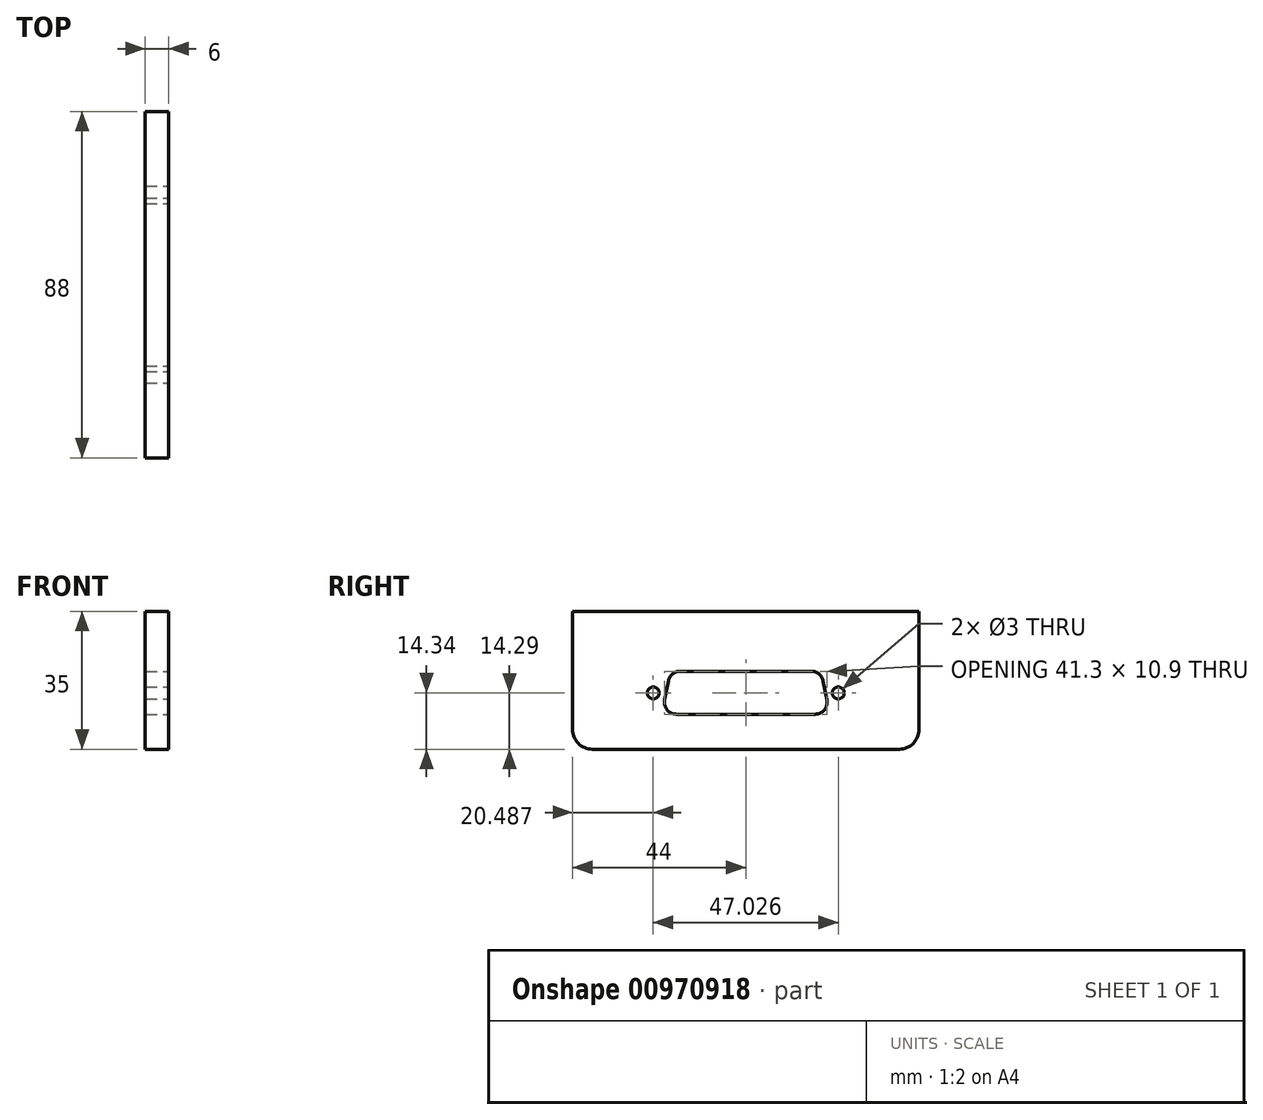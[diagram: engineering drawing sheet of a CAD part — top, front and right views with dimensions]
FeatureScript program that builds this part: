
annotation { "Feature Type Name" : "Feature", "Feature Type Description" : "" }
export const myFeature = defineFeature(function(context is Context, id is Id, definition is map)
    precondition{}
    {
        {
            var Q0;
            Q0=qCreatedBy(makeId("Right.planeOp"),FACE);
            var sketch = newSketch(context, id + "F0", { "sketchPlane" : qUnion([Q0])});
            skLineSegment(sketch, "E0", {"start": v(-81, 2.43) * mm, "end": v(-84.5, 2.43) * mm});
            skLineSegment(sketch, "E1", {"start": v(-84.5, 2.43) * mm, "end": v(-84.5, -12.07) * mm});
            skLineSegment(sketch, "E2", {"start": v(-84.5, -19.57) * mm, "end": v(-84.5, -27.57) * mm});
            skLineSegment(sketch, "E3", {"start": v(-79.5, -32.57) * mm, "end": v(-1.5, -32.57) * mm});
            skLineSegment(sketch, "E4", {"start": v(-81, -29.07) * mm, "end": v(0, -29.07) * mm, "construction": true});
            skLineSegment(sketch, "E5", {"start": v(3.5, 2.43) * mm, "end": v(0, 2.43) * mm});
            skPoint(sketch, "E6.visualSharp", {"position": v(-84.5, -32.57) * mm});
            skArc(sketch, "E6.filletArc", {"start": v(-84.5, -27.57) * mm, "mid": v(-83.04, -31.1) * mm, "end": v(-79.5, -32.57) * mm});
            skLineSegment(sketch, "E7", {"start": v(3.5, 2.43) * mm, "end": v(3.5, -10.57) * mm});
            skLineSegment(sketch, "E8", {"start": v(3.5, -27.57) * mm, "end": v(3.5, -19.57) * mm});
            skLineSegment(sketch, "E9", {"start": v(0, 2.43) * mm, "end": v(0, -29.07) * mm, "construction": true});
            skLineSegment(sketch, "E10", {"start": v(-81, 2.43) * mm, "end": v(0, 2.43) * mm});
            skLineSegment(sketch, "E11", {"start": v(-84.5, -12.07) * mm, "end": v(-84.5, -19.57) * mm});
            skLineSegment(sketch, "E12", {"start": v(3.5, -10.57) * mm, "end": v(3.5, -19.57) * mm});
            skPoint(sketch, "E13.visualSharp", {"position": v(3.5, -32.57) * mm});
            skArc(sketch, "E13.filletArc", {"start": v(-1.5, -32.57) * mm, "mid": v(2.04, -31.1) * mm, "end": v(3.5, -27.57) * mm});
            skLineSegment(sketch, "E14", {"start": v(-81, -29.07) * mm, "end": v(-81, 2.43) * mm, "construction": true});
            skLineSegment(sketch, "E15", {"start": v(-67.01, -12.08) * mm, "end": v(-67.01, -24.48) * mm});
            skLineSegment(sketch, "E16", {"start": v(-67.01, -24.48) * mm, "end": v(-13.99, -24.48) * mm});
            skLineSegment(sketch, "E17", {"start": v(-13.99, -24.48) * mm, "end": v(-13.99, -12.07) * mm});
            skLineSegment(sketch, "E18", {"start": v(-13.99, -12.07) * mm, "end": v(-66.49, -12.07) * mm});
            skCircle(sketch, "E19", {"center": v(-64.01, -18.28) * mm, "radius": 1.5 * mm});
            skLineSegment(sketch, "E20", {"start": v(-40.5, -24.48) * mm, "end": v(-40.5, -12.07) * mm, "construction": true});
            skCircle(sketch, "E21.MirrorC", {"center": v(-16.99, -18.28) * mm, "radius": 1.5 * mm});
            skLineSegment(sketch, "E22", {"start": v(-60.15, -15.21) * mm, "end": v(-61.1, -20.11) * mm});
            skLineSegment(sketch, "E23.MirrorCS", {"start": v(-20.85, -15.21) * mm, "end": v(-19.9, -20.11) * mm});
            skLineSegment(sketch, "E24", {"start": v(-57.2, -12.78) * mm, "end": v(-23.8, -12.78) * mm});
            skLineSegment(sketch, "E25", {"start": v(-22.85, -23.68) * mm, "end": v(-58.15, -23.68) * mm});
            skPoint(sketch, "E26.visualSharp", {"position": v(-59.68, -12.78) * mm});
            skArc(sketch, "E26.filletArc", {"start": v(-57.2, -12.78) * mm, "mid": v(-59.11, -13.47) * mm, "end": v(-60.15, -15.21) * mm});
            skPoint(sketch, "E27.visualSharp", {"position": v(-61.78, -23.68) * mm});
            skArc(sketch, "E27.filletArc", {"start": v(-61.1, -20.11) * mm, "mid": v(-60.46, -22.6) * mm, "end": v(-58.15, -23.68) * mm});
            skPoint(sketch, "E28.visualSharp", {"position": v(-21.32, -12.78) * mm});
            skArc(sketch, "E28.filletArc", {"start": v(-20.85, -15.21) * mm, "mid": v(-21.89, -13.47) * mm, "end": v(-23.8, -12.78) * mm});
            skPoint(sketch, "E29.visualSharp", {"position": v(-19.22, -23.68) * mm});
            skArc(sketch, "E29.filletArc", {"start": v(-22.85, -23.68) * mm, "mid": v(-20.54, -22.6) * mm, "end": v(-19.9, -20.11) * mm});
            skSolve(sketch);
        }
        {
            var Q0;
            Q0=makeQuery(id+"F0.imprint","IMPRINT",FACE,{"disambiguationData":[TD([[makeQuery(id+"F0.imprint","IMPRINT",EDGE,{"derivedFrom":sQuery(id+"F0.wireOp",EDGE,"E0")}),1.0]])]});
            extrude(context, id + "F1", {"entities" : qUnion([Q0]), "oppositeDirection" : true, "depth" : 6 * mm, "offsetDistance" : 25 * mm});
        }
    });
